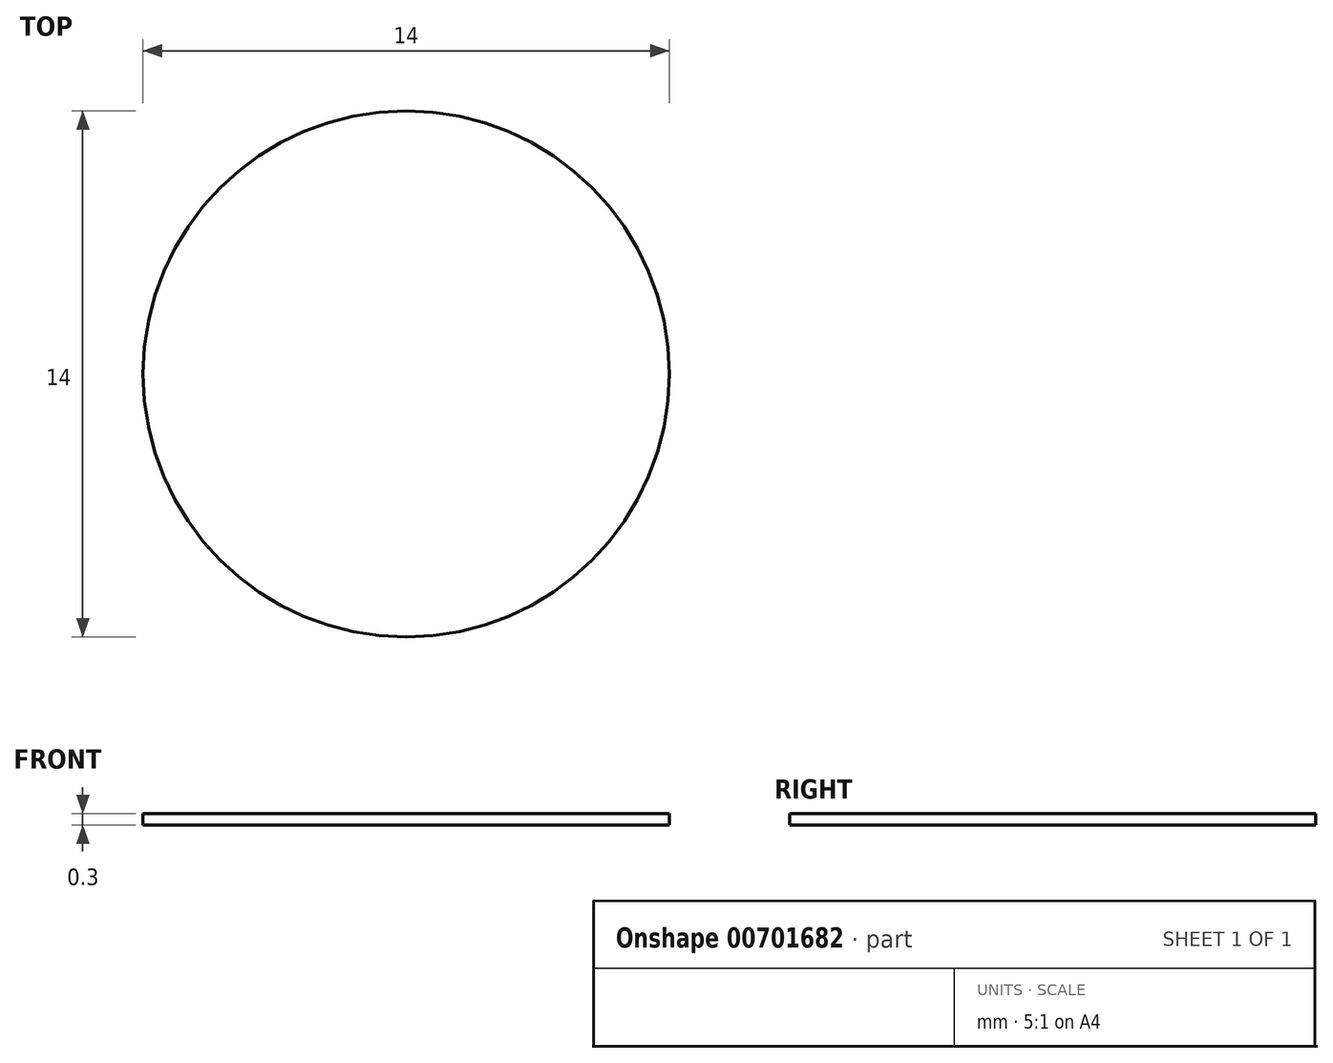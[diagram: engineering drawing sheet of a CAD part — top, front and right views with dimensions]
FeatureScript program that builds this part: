
annotation { "Feature Type Name" : "Feature", "Feature Type Description" : "" }
export const myFeature = defineFeature(function(context is Context, id is Id, definition is map)
    precondition{}
    {
        {
            var Q0;
            Q0=qCreatedBy(makeId("Top.planeOp"),FACE);
            var sketch = newSketch(context, id + "F0", { "sketchPlane" : qUnion([Q0])});
            skCircle(sketch, "E0", {"center": v(0, 0) * mm, "radius": 7 * mm});
            skSolve(sketch);
        }
        {
            var Q0;
            Q0=makeQuery(id+"F0.imprint","IMPRINT",FACE,{"disambiguationData":[TD([[makeQuery(id+"F0.imprint","IMPRINT",EDGE,{"derivedFrom":sQuery(id+"F0.wireOp",EDGE,"E0")}),1.0]])]});
            extrude(context, id + "F1", {"entities" : qUnion([Q0]), "depth" : 0.3 * mm, "offsetDistance" : 25 * mm});
        }
    });
